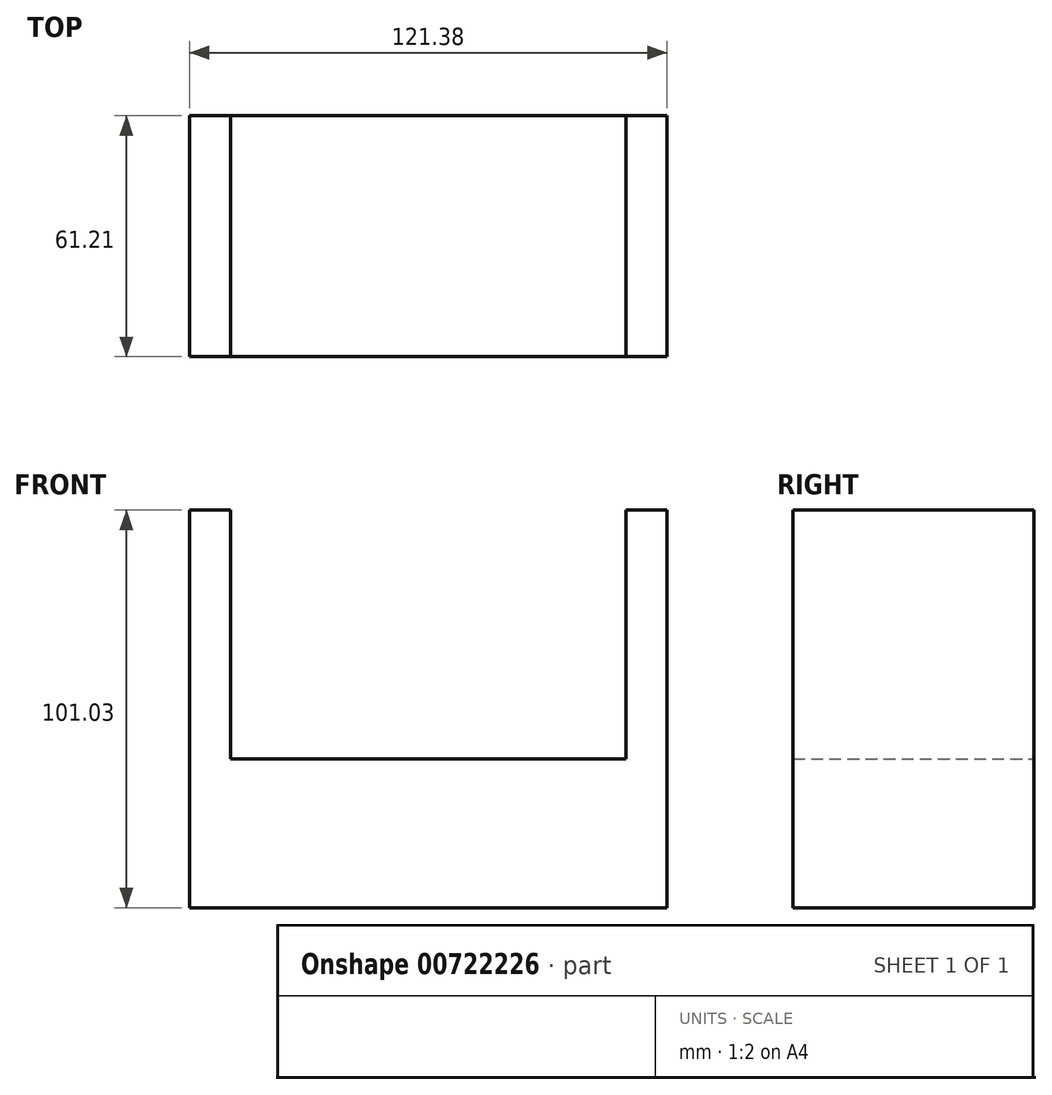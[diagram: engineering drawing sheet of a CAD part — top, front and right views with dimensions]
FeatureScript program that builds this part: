
annotation { "Feature Type Name" : "Feature", "Feature Type Description" : "" }
export const myFeature = defineFeature(function(context is Context, id is Id, definition is map)
    precondition{}
    {
        {
            var Q0;
            Q0=qCreatedBy(makeId("Front.planeOp"),FACE);
            var sketch = newSketch(context, id + "F0", { "sketchPlane" : qUnion([Q0])});
            skLineSegment(sketch, "E0", {"start": v(-55.04, -37.86) * mm, "end": v(66.34, -37.86) * mm});
            skLineSegment(sketch, "E1", {"start": v(66.34, -37.86) * mm, "end": v(66.34, 63.17) * mm});
            skLineSegment(sketch, "E2", {"start": v(-55.04, -37.86) * mm, "end": v(-55.04, 63.17) * mm});
            skLineSegment(sketch, "E3", {"start": v(-55.04, 63.17) * mm, "end": v(-44.64, 63.17) * mm});
            skLineSegment(sketch, "E4", {"start": v(-44.64, 63.17) * mm, "end": v(-44.64, 0) * mm});
            skLineSegment(sketch, "E5", {"start": v(-44.64, 0) * mm, "end": v(55.94, 0) * mm});
            skLineSegment(sketch, "E6", {"start": v(55.94, 0) * mm, "end": v(55.94, 63.17) * mm});
            skLineSegment(sketch, "E7", {"start": v(55.94, 63.17) * mm, "end": v(66.34, 63.17) * mm});
            skSolve(sketch);
        }
        {
            var Q0;
            Q0 = qSketchRegion(id + "F0", true);
            extrude(context, id + "F1", {"entities" : qUnion([Q0]), "depth" : 61.2 * mm, "offsetDistance" : 25.4 * mm});
        }
    });
